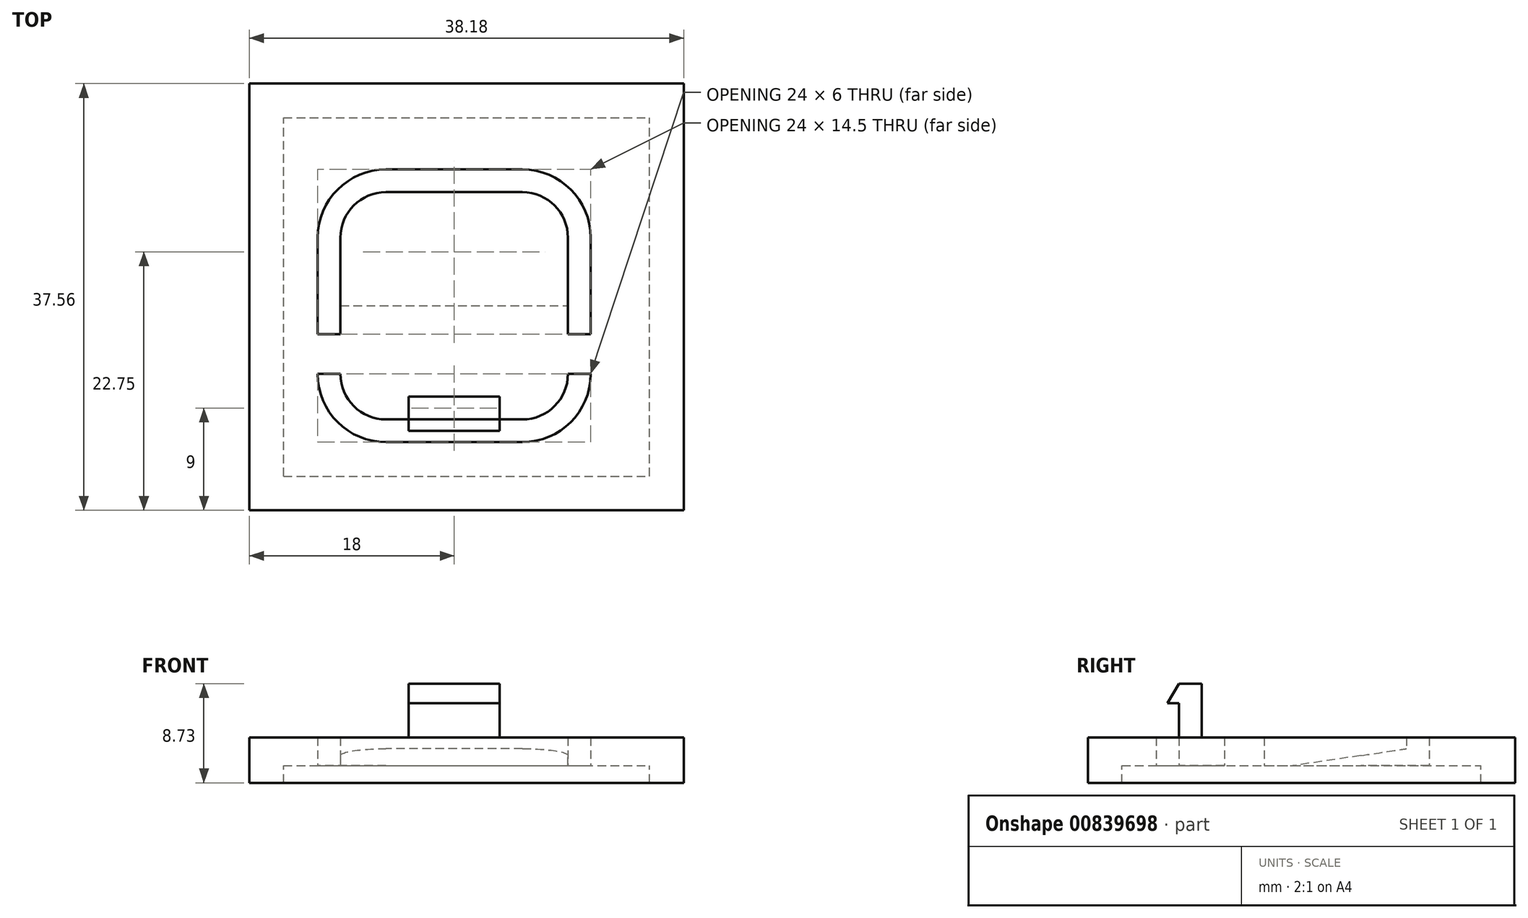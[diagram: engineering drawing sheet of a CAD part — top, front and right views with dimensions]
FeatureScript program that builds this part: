
annotation { "Feature Type Name" : "Feature", "Feature Type Description" : "" }
export const myFeature = defineFeature(function(context is Context, id is Id, definition is map)
    precondition{}
    {
        {
            var Q0;
            Q0=qCreatedBy(makeId("Top.planeOp"),FACE);
            var sketch = newSketch(context, id + "F0", { "sketchPlane" : qUnion([Q0])});
            skLineSegment(sketch, "E0.bottom", {"start": v(0, 0) * mm, "end": v(38.18, 0) * mm});
            skLineSegment(sketch, "E0.top", {"start": v(0, 37.56) * mm, "end": v(38.18, 37.56) * mm});
            skLineSegment(sketch, "E0.left", {"start": v(0, 0) * mm, "end": v(0, 37.56) * mm});
            skLineSegment(sketch, "E0.right", {"start": v(38.18, 0) * mm, "end": v(38.18, 37.56) * mm});
            skLineSegment(sketch, "E1.bottom", {"start": v(12, 8) * mm, "end": v(24, 8) * mm});
            skLineSegment(sketch, "E1.top", {"start": v(12, 28) * mm, "end": v(24, 28) * mm});
            skPoint(sketch, "E2.visualSharp", {"position": v(8.04, 28) * mm});
            skArc(sketch, "E2.filletArc", {"start": v(12, 28) * mm, "mid": v(9.17, 26.83) * mm, "end": v(8, 24) * mm});
            skPoint(sketch, "E3.visualSharp", {"position": v(28.04, 28) * mm});
            skArc(sketch, "E3.filletArc", {"start": v(28, 24) * mm, "mid": v(26.83, 26.83) * mm, "end": v(24, 28) * mm});
            skPoint(sketch, "E4.visualSharp", {"position": v(28.04, 8) * mm});
            skArc(sketch, "E4.filletArc", {"start": v(24, 8) * mm, "mid": v(26.83, 9.17) * mm, "end": v(28, 12) * mm});
            skPoint(sketch, "E5.visualSharp", {"position": v(8.04, 8) * mm});
            skArc(sketch, "E5.filletArc", {"start": v(8, 12) * mm, "mid": v(9.17, 9.17) * mm, "end": v(12, 8) * mm});
            skArc(sketch, "E6.1", {"start": v(12, 30) * mm, "mid": v(7.76, 28.24) * mm, "end": v(6, 24) * mm});
            skArc(sketch, "E6.2", {"start": v(6, 12) * mm, "mid": v(7.76, 7.76) * mm, "end": v(12, 6) * mm});
            skLineSegment(sketch, "E6.3", {"start": v(12, 30) * mm, "end": v(24, 30) * mm});
            skLineSegment(sketch, "E6.4", {"start": v(12, 6) * mm, "end": v(24, 6) * mm});
            skArc(sketch, "E6.5", {"start": v(24, 6) * mm, "mid": v(28.24, 7.76) * mm, "end": v(30, 12) * mm});
            skArc(sketch, "E6.7", {"start": v(30, 24) * mm, "mid": v(28.24, 28.24) * mm, "end": v(24, 30) * mm});
            skLineSegment(sketch, "E7", {"start": v(6, 12) * mm, "end": v(8, 12) * mm});
            skLineSegment(sketch, "E8", {"start": v(28, 12) * mm, "end": v(30, 12) * mm});
            skLineSegment(sketch, "E9", {"start": v(30, 15.5) * mm, "end": v(28, 15.5) * mm});
            skLineSegment(sketch, "E10", {"start": v(28, 15.5) * mm, "end": v(8, 15.5) * mm, "construction": true});
            skLineSegment(sketch, "E11", {"start": v(8, 15.5) * mm, "end": v(6, 15.5) * mm});
            skLineSegment(sketch, "E12", {"start": v(8, 15.5) * mm, "end": v(8, 24) * mm});
            skLineSegment(sketch, "E13", {"start": v(6, 15.5) * mm, "end": v(6, 24) * mm});
            skLineSegment(sketch, "E14", {"start": v(28, 15.5) * mm, "end": v(28, 24) * mm});
            skLineSegment(sketch, "E15", {"start": v(30, 15.5) * mm, "end": v(30, 24) * mm});
            skLineSegment(sketch, "E16", {"start": v(28, 15.5) * mm, "end": v(28, 12) * mm, "construction": true});
            skLineSegment(sketch, "E17", {"start": v(30, 15.5) * mm, "end": v(30, 12) * mm, "construction": true});
            skLineSegment(sketch, "E18", {"start": v(8, 15.5) * mm, "end": v(8, 12) * mm, "construction": true});
            skLineSegment(sketch, "E19", {"start": v(6, 15.5) * mm, "end": v(6, 12) * mm, "construction": true});
            skSolve(sketch);
        }
        {
            var Q0;
            Q0 = qSketchRegion(id + "F0", true);
            extrude(context, id + "F1", {"entities" : qUnion([Q0]), "depth" : 2.5 * mm, "offsetDistance" : 25 * mm});
        }
        {
            var Q0;
            Q0=makeQuery(id+"F1.opExtrude","CAP_FACE",FACE,{"disambiguationData":[OSD([sQuery(id+"F0.wireOp",EDGE,"E0.bottom"),sQuery(id+"F0.wireOp",EDGE,"E0.top"),sQuery(id+"F0.wireOp",EDGE,"E0.left"),sQuery(id+"F0.wireOp",EDGE,"E0.right"),sQuery(id+"F0.wireOp",EDGE,"E1.bottom"),sQuery(id+"F0.wireOp",EDGE,"E1.top"),sQuery(id+"F0.wireOp",EDGE,"E2.filletArc"),sQuery(id+"F0.wireOp",EDGE,"E3.filletArc"),sQuery(id+"F0.wireOp",EDGE,"E4.filletArc"),sQuery(id+"F0.wireOp",EDGE,"E5.filletArc"),sQuery(id+"F0.wireOp",EDGE,"E6.1"),sQuery(id+"F0.wireOp",EDGE,"E6.2"),sQuery(id+"F0.wireOp",EDGE,"E6.3"),sQuery(id+"F0.wireOp",EDGE,"E6.4"),sQuery(id+"F0.wireOp",EDGE,"E6.5"),sQuery(id+"F0.wireOp",EDGE,"E6.7"),sQuery(id+"F0.wireOp",EDGE,"E7"),sQuery(id+"F0.wireOp",EDGE,"E8"),sQuery(id+"F0.wireOp",EDGE,"E9"),sQuery(id+"F0.wireOp",EDGE,"E11"),sQuery(id+"F0.wireOp",EDGE,"E12"),sQuery(id+"F0.wireOp",EDGE,"E13"),sQuery(id+"F0.wireOp",EDGE,"E14"),sQuery(id+"F0.wireOp",EDGE,"E15")])],"isStart":true});
            var sketch = newSketch(context, id + "F2", { "sketchPlane" : qUnion([Q0])});
            skLineSegment(sketch, "E20.0", {"start": v(38.18, 0) * mm, "end": v(38.18, -37.56) * mm});
            skLineSegment(sketch, "E20.1", {"start": v(0, -37.56) * mm, "end": v(38.18, -37.56) * mm});
            skLineSegment(sketch, "E20.2", {"start": v(0, 0) * mm, "end": v(0, -37.56) * mm});
            skLineSegment(sketch, "E20.3", {"start": v(0, 0) * mm, "end": v(38.18, 0) * mm});
            skLineSegment(sketch, "E21.0", {"start": v(3, -3) * mm, "end": v(35.18, -3) * mm});
            skLineSegment(sketch, "E21.1", {"start": v(3, -3) * mm, "end": v(3, -34.56) * mm});
            skLineSegment(sketch, "E21.2", {"start": v(3, -34.56) * mm, "end": v(35.18, -34.56) * mm});
            skLineSegment(sketch, "E21.3", {"start": v(35.18, -3) * mm, "end": v(35.18, -34.56) * mm});
            skSolve(sketch);
        }
        {
            var Q0;
            Q0 = qSketchRegion(id + "F2", true);
            extrude(context, id + "F3", {"entities" : qUnion([Q0]), "operationType" : NewBodyOperationType.ADD, "depth" : 1.5 * mm, "offsetDistance" : 25 * mm});
        }
        {
            var Q0;
            Q0=qCreatedBy(makeId("Right.planeOp"),FACE);
            var sketch = newSketch(context, id + "F4", { "sketchPlane" : qUnion([Q0])});
            skPoint(sketch, "E22.0", {"position": v(8, 2.5) * mm});
            skLineSegment(sketch, "E23", {"start": v(8, 2.5) * mm, "end": v(8, 5.5) * mm});
            skLineSegment(sketch, "E24", {"start": v(8, 5.5) * mm, "end": v(7, 5.5) * mm});
            skLineSegment(sketch, "E25", {"start": v(7, 5.5) * mm, "end": v(8, 7.23) * mm});
            skLineSegment(sketch, "E26", {"start": v(8, 7.23) * mm, "end": v(10, 7.23) * mm});
            skLineSegment(sketch, "E27", {"start": v(10, 7.23) * mm, "end": v(10, 2.5) * mm});
            skLineSegment(sketch, "E28", {"start": v(10, 2.5) * mm, "end": v(8, 2.5) * mm});
            skSolve(sketch);
        }
        {
            var Q0;
            Q0 = qSketchRegion(id + "F4", true);
            extrude(context, id + "F5", {"entities" : qUnion([Q0]), "operationType" : NewBodyOperationType.ADD, "depth" : 22 * mm, "offsetDistance" : 25 * mm});
        }
        {
            var Q0;
            Q0 = qSketchRegion(id + "F4", true);
            extrude(context, id + "F6", {"entities" : qUnion([Q0]), "operationType" : NewBodyOperationType.REMOVE, "depth" : 14 * mm, "offsetDistance" : 25 * mm});
        }
        {
            var Q0;
            Q0=makeQuery(id+"F1.opExtrude","CAP_EDGE",EDGE,{"disambiguationData":[OSD([sQuery(id+"F0.wireOp",EDGE,"E1.top")])],"isStart":true});
            chamfer(context, id + "F7", {"entities" : qUnion([Q0]), "chamferType" : ChamferType.TWO_OFFSETS, "width1" : 10 * mm, "oppositeDirection" : false, "width2" : 1.5 * mm});
        }
    });
